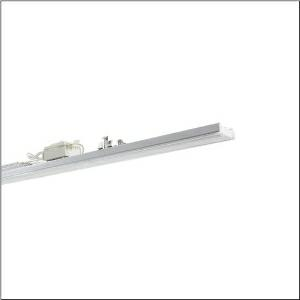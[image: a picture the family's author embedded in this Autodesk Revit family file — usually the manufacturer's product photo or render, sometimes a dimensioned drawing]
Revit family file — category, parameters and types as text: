
# Revit family: licross_r__21_recessed_mo_52te12dv6fxg_61b3
name_source: partatom
category: Lighting Fixtures
units: mm (PartAtom-declared; Revit-internal decimal feet)

## family parameters
Cut with Voids When Loaded = No
Host = Face
Light Source = No
Part Type = Normal
Room Calculation Point = No
Round Connector Dimension = Use Diameter
Shared = No

## types (1)
- --- (1 x LED, 15000 lm, 85.3 W, 6500K)
    Apparent Load = 85 VA
    CIE Flux Codes = 72 92 99 100 100
    Color Rendering = 80
    Color Temperature = 6500K
    Default Elevation = 1800 mm
    Description = Licross® 21 Recessed MO, luminaire insert, of sheet steel, galvanised, coil coated, white, length: 2.250mm, width: 66mm, height: 67mm, LED rated luminous flux: 15.000lm, light colour: 865, control gear: DALI 2, with plug, 5-pole, with phase selection, mains connection: 220..240V, AC, 50/60Hz, rated input power: 85W, halogen-free wiring, primary optical cover: cover, of PMMA, light emission: direct distribution, primary light characteristic: symmetric, protection rating (complete): IP54, insulation class (complete): insulation class I (protective earthing), certification: CE, ENEC, VDE, UKCA, protection symbol: D if used in an environment with non-conductive dust loads with corresponding accessories, impact resistance: IK06, permissible ambient temperature for indoor applications: -25..+35°C, corresponds to IFS (International Featured Standards) requirements for safety and quality in the food industry, reducing of maximum allowable ambient temperature of 5°C with ceiling mounting, LABS conformity tested according to VDMA 24364:2018-05, packaging unit: 1 piece
    Height = 58 mm
    Lamp = 1 x LED
    Lamp Light Flux = 15000 lm
    Lamp Power = 85.3 W
    Lamp count = 1
    Length = 2250 mm
    Luminous efficacy = 176 lm/W
    Manufacturer = Siteco
    ModVariant = No
    Model = 52TE12DV6FXG
    Mounting Place = Ceiling
    Mounting Type = Pendant
    Number of Poles = 1
    OnlyDefault = Yes
    Power Factor = 1
    Product Name = Licross® 21 Recessed MO
    Product group = luminaire insert
    ProductGroupID = 902
    Protection Class = Protection class I
    Protection Degree = IP 54
    RLX_Detail_Level = 1
    RLX_Emergency_Light_Flux = 0 lm
    RLX_Emergency_Type = 0
    RLX_Emergency_Type_DB = No
    RlxData = <blob elided: 29797 chars, md5=2551240a>
    Socket = socket
    Standby Power = 0 W
    System Light Flux = 15000 lm
    System Power = 85 W
    Type Comments = factory setting: luminous flux: 100 % | dim-lin: 254 | 390 mA
    Type Image = l_1296930.jpg
    URL = http://relux.com
    VarID = @adj_089488
    Voltage = 0 V
    Weight = 0.00 kg
    Width = 66 mm

## geometry (parser evidence)
native form markers: Blend x4, Sweep x9
no freeform markers — native parametric forms only
